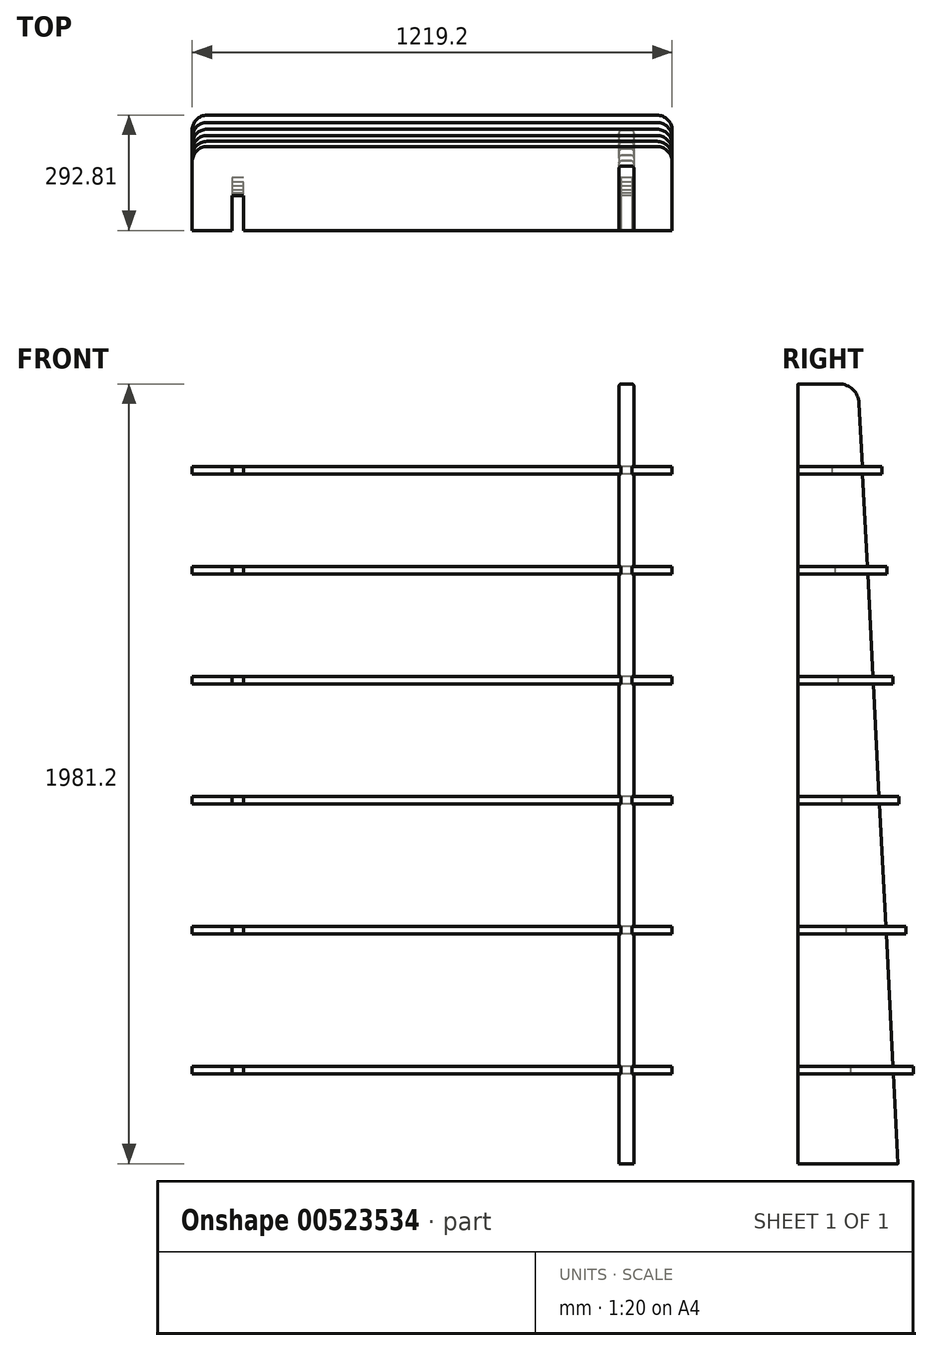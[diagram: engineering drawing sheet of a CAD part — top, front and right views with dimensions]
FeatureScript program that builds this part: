
annotation { "Feature Type Name" : "Feature", "Feature Type Description" : "" }
export const myFeature = defineFeature(function(context is Context, id is Id, definition is map)
    precondition{}
    {
        {
            var Q0;
            Q0=qCreatedBy(makeId("Right.planeOp"),FACE);
            var sketch = newSketch(context, id + "F0", { "sketchPlane" : qUnion([Q0])});
            skLineSegment(sketch, "E0.bottom", {"start": v(-186.04, 1286.69) * mm, "end": v(-81.9, 1286.69) * mm});
            skLineSegment(sketch, "E0.top", {"start": v(-186.04, -694.51) * mm, "end": v(67.96, -694.51) * mm});
            skLineSegment(sketch, "E0.left", {"start": v(-186.04, 1286.69) * mm, "end": v(-186.04, -694.51) * mm});
            skLineSegment(sketch, "E1", {"start": v(56.23, -465.91) * mm, "end": v(-51.72, -465.91) * mm});
            skLineSegment(sketch, "E2", {"start": v(-51.72, -465.91) * mm, "end": v(-51.72, -446.86) * mm});
            skLineSegment(sketch, "E3", {"start": v(-51.72, -446.86) * mm, "end": v(55.26, -446.86) * mm});
            skLineSegment(sketch, "E4.0.1.0", {"start": v(-63.6, -110.31) * mm, "end": v(-63.6, -91.26) * mm});
            skLineSegment(sketch, "E4.0.1.1", {"start": v(38, -110.31) * mm, "end": v(-63.6, -110.31) * mm});
            skLineSegment(sketch, "E4.0.1.2", {"start": v(-63.6, -91.26) * mm, "end": v(37.02, -91.26) * mm});
            skLineSegment(sketch, "E4.0.2.0", {"start": v(-74.19, 219.89) * mm, "end": v(-74.19, 238.94) * mm});
            skLineSegment(sketch, "E4.0.2.1", {"start": v(21.06, 219.89) * mm, "end": v(-74.19, 219.89) * mm});
            skLineSegment(sketch, "E4.0.2.2", {"start": v(-74.19, 238.94) * mm, "end": v(20.09, 238.94) * mm});
            skLineSegment(sketch, "E4.0.3.0", {"start": v(-83.47, 524.69) * mm, "end": v(-83.47, 543.74) * mm});
            skLineSegment(sketch, "E4.0.3.1", {"start": v(5.43, 524.69) * mm, "end": v(-83.47, 524.69) * mm});
            skLineSegment(sketch, "E4.0.3.2", {"start": v(-83.47, 543.74) * mm, "end": v(4.46, 543.74) * mm});
            skLineSegment(sketch, "E4.0.4.0", {"start": v(-91.44, 804.09) * mm, "end": v(-91.44, 823.14) * mm});
            skLineSegment(sketch, "E4.0.4.1", {"start": v(-8.9, 804.09) * mm, "end": v(-91.44, 804.09) * mm});
            skLineSegment(sketch, "E4.0.4.2", {"start": v(-91.44, 823.14) * mm, "end": v(-9.87, 823.14) * mm});
            skLineSegment(sketch, "E4.0.5.0", {"start": v(-98.12, 1058.09) * mm, "end": v(-98.12, 1077.14) * mm});
            skLineSegment(sketch, "E4.0.5.1", {"start": v(-21.92, 1058.09) * mm, "end": v(-98.12, 1058.09) * mm});
            skLineSegment(sketch, "E4.0.5.2", {"start": v(-98.12, 1077.14) * mm, "end": v(-22.9, 1077.14) * mm});
            skLineSegment(sketch, "E5", {"start": v(67.96, -694.51) * mm, "end": v(56.23, -465.91) * mm});
            skLineSegment(sketch, "E6.trimOffspring", {"start": v(-22.9, 1077.14) * mm, "end": v(-31.17, 1238.49) * mm});
            skLineSegment(sketch, "E7.trimOffspring", {"start": v(-9.87, 823.14) * mm, "end": v(-21.92, 1058.09) * mm});
            skLineSegment(sketch, "E8.trimOffspring", {"start": v(4.46, 543.74) * mm, "end": v(-8.9, 804.09) * mm});
            skLineSegment(sketch, "E9.trimOffspring", {"start": v(20.09, 238.94) * mm, "end": v(5.43, 524.69) * mm});
            skLineSegment(sketch, "E10.trimOffspring", {"start": v(37.02, -91.26) * mm, "end": v(21.06, 219.89) * mm});
            skLineSegment(sketch, "E11.trimOffspring", {"start": v(55.26, -446.86) * mm, "end": v(38, -110.31) * mm});
            skPoint(sketch, "E12.visualSharp", {"position": v(-33.64, 1286.69) * mm});
            skArc(sketch, "E12.filletArc", {"start": v(-31.17, 1238.49) * mm, "mid": v(-46.92, 1272.72) * mm, "end": v(-81.9, 1286.69) * mm});
            skSolve(sketch);
        }
        {
            var Q0;
            Q0 = qSketchRegion(id + "F0", true);
            extrude(context, id + "F1", {"entities" : qUnion([Q0]), "depth" : 38.1 * mm, "offsetDistance" : 25.4 * mm});
        }
        {
            var Q0;
            Q0=makeQuery(id+"F1.opExtrude","SWEPT_FACE",FACE,{"disambiguationData":[OSD([sQuery(id+"F0.wireOp",EDGE,"E0.left")])]});
            var sketch = newSketch(context, id + "F2", { "sketchPlane" : qUnion([Q0])});
            skLineSegment(sketch, "E13.bottom", {"start": v(0, 1077.14) * mm, "end": v(4.76, 1077.14) * mm});
            skLineSegment(sketch, "E13.top", {"start": v(0, 1058.09) * mm, "end": v(4.76, 1058.09) * mm});
            skLineSegment(sketch, "E13.left", {"start": v(0, 1077.14) * mm, "end": v(0, 1058.09) * mm});
            skLineSegment(sketch, "E13.right", {"start": v(4.76, 1077.14) * mm, "end": v(4.76, 1058.09) * mm});
            skLineSegment(sketch, "E14.bottom", {"start": v(0, 823.14) * mm, "end": v(4.76, 823.14) * mm});
            skLineSegment(sketch, "E14.top", {"start": v(0, 804.09) * mm, "end": v(4.76, 804.09) * mm});
            skLineSegment(sketch, "E14.left", {"start": v(0, 823.14) * mm, "end": v(0, 804.09) * mm});
            skLineSegment(sketch, "E14.right", {"start": v(4.76, 823.14) * mm, "end": v(4.76, 804.09) * mm});
            skLineSegment(sketch, "E15.bottom", {"start": v(0, 543.74) * mm, "end": v(4.76, 543.74) * mm});
            skLineSegment(sketch, "E15.top", {"start": v(0, 524.69) * mm, "end": v(4.76, 524.69) * mm});
            skLineSegment(sketch, "E15.left", {"start": v(0, 543.74) * mm, "end": v(0, 524.69) * mm});
            skLineSegment(sketch, "E15.right", {"start": v(4.76, 543.74) * mm, "end": v(4.76, 524.69) * mm});
            skLineSegment(sketch, "E16.bottom", {"start": v(0, 238.94) * mm, "end": v(4.76, 238.94) * mm});
            skLineSegment(sketch, "E16.top", {"start": v(0, 219.89) * mm, "end": v(4.76, 219.89) * mm});
            skLineSegment(sketch, "E16.left", {"start": v(0, 238.94) * mm, "end": v(0, 219.89) * mm});
            skLineSegment(sketch, "E16.right", {"start": v(4.76, 238.94) * mm, "end": v(4.76, 219.89) * mm});
            skLineSegment(sketch, "E17.bottom", {"start": v(0, -91.26) * mm, "end": v(4.76, -91.26) * mm});
            skLineSegment(sketch, "E17.top", {"start": v(0, -110.31) * mm, "end": v(4.76, -110.31) * mm});
            skLineSegment(sketch, "E17.left", {"start": v(0, -91.26) * mm, "end": v(0, -110.31) * mm});
            skLineSegment(sketch, "E17.right", {"start": v(4.76, -91.26) * mm, "end": v(4.76, -110.31) * mm});
            skLineSegment(sketch, "E18.bottom", {"start": v(0, -446.86) * mm, "end": v(4.76, -446.86) * mm});
            skLineSegment(sketch, "E18.top", {"start": v(0, -465.91) * mm, "end": v(4.76, -465.91) * mm});
            skLineSegment(sketch, "E18.left", {"start": v(0, -446.86) * mm, "end": v(0, -465.91) * mm});
            skLineSegment(sketch, "E18.right", {"start": v(4.76, -446.86) * mm, "end": v(4.76, -465.91) * mm});
            skLineSegment(sketch, "E19", {"start": v(19.05, 1286.69) * mm, "end": v(19.05, -694.51) * mm, "construction": true});
            skLineSegment(sketch, "E20.MirrorCS", {"start": v(38.1, -465.91) * mm, "end": v(33.34, -465.91) * mm});
            skLineSegment(sketch, "E21.MirrorCS", {"start": v(38.1, -446.86) * mm, "end": v(33.34, -446.86) * mm});
            skLineSegment(sketch, "E22.MirrorCS", {"start": v(33.34, -446.86) * mm, "end": v(33.34, -465.91) * mm});
            skLineSegment(sketch, "E23.MirrorCS", {"start": v(38.1, -446.86) * mm, "end": v(38.1, -465.91) * mm});
            skLineSegment(sketch, "E24.MirrorCS", {"start": v(38.1, -110.31) * mm, "end": v(33.34, -110.31) * mm});
            skLineSegment(sketch, "E25.MirrorCS", {"start": v(38.1, -91.26) * mm, "end": v(33.34, -91.26) * mm});
            skLineSegment(sketch, "E26.MirrorCS", {"start": v(33.34, -91.26) * mm, "end": v(33.34, -110.31) * mm});
            skLineSegment(sketch, "E27.MirrorCS", {"start": v(38.1, -91.26) * mm, "end": v(38.1, -110.31) * mm});
            skLineSegment(sketch, "E28.MirrorCS", {"start": v(38.1, 219.89) * mm, "end": v(33.34, 219.89) * mm});
            skLineSegment(sketch, "E29.MirrorCS", {"start": v(38.1, 238.94) * mm, "end": v(33.34, 238.94) * mm});
            skLineSegment(sketch, "E30.MirrorCS", {"start": v(38.1, 238.94) * mm, "end": v(38.1, 219.89) * mm});
            skLineSegment(sketch, "E31.MirrorCS", {"start": v(33.34, 238.94) * mm, "end": v(33.34, 219.89) * mm});
            skLineSegment(sketch, "E32.MirrorCS", {"start": v(38.1, 543.74) * mm, "end": v(33.34, 543.74) * mm});
            skLineSegment(sketch, "E33.MirrorCS", {"start": v(38.1, 524.69) * mm, "end": v(33.34, 524.69) * mm});
            skLineSegment(sketch, "E34.MirrorCS", {"start": v(38.1, 543.74) * mm, "end": v(38.1, 524.69) * mm});
            skLineSegment(sketch, "E35.MirrorCS", {"start": v(33.34, 543.74) * mm, "end": v(33.34, 524.69) * mm});
            skLineSegment(sketch, "E36.MirrorCS", {"start": v(38.1, 823.14) * mm, "end": v(33.34, 823.14) * mm});
            skLineSegment(sketch, "E37.MirrorCS", {"start": v(38.1, 804.09) * mm, "end": v(33.34, 804.09) * mm});
            skLineSegment(sketch, "E38.MirrorCS", {"start": v(38.1, 823.14) * mm, "end": v(38.1, 804.09) * mm});
            skLineSegment(sketch, "E39.MirrorCS", {"start": v(33.34, 823.14) * mm, "end": v(33.34, 804.09) * mm});
            skLineSegment(sketch, "E40.MirrorCS", {"start": v(38.1, 1077.14) * mm, "end": v(33.34, 1077.14) * mm});
            skLineSegment(sketch, "E41.MirrorCS", {"start": v(38.1, 1058.09) * mm, "end": v(33.34, 1058.09) * mm});
            skLineSegment(sketch, "E42.MirrorCS", {"start": v(33.34, 1077.14) * mm, "end": v(33.34, 1058.09) * mm});
            skLineSegment(sketch, "E43.MirrorCS", {"start": v(38.1, 1077.14) * mm, "end": v(38.1, 1058.09) * mm});
            skSolve(sketch);
        }
        {
            var Q0;
            Q0 = qSketchRegion(id + "F2", true);
            extrude(context, id + "F3", {"entities" : qUnion([Q0]), "operationType" : NewBodyOperationType.REMOVE, "endBound" : BoundingType.UP_TO_NEXT, "oppositeDirection" : true, "depth" : 25.4 * mm, "offsetDistance" : 25.4 * mm});
        }
        {
            var Q0;
            Q0=makeQuery(id+"F3.boolean.opBoolean","MERGE",FACE,{"derivedFrom":[makeQuery(id+"F1.opExtrude","SWEPT_FACE",FACE,{"disambiguationData":[OSD([sQuery(id+"F0.wireOp",EDGE,"E1")])]}),makeQuery(id+"F3.opExtrude","SWEPT_FACE",FACE,{"disambiguationData":[OSD([sQuery(id+"F2.wireOp",EDGE,"E18.top")])]}),makeQuery(id+"F3.opExtrude","SWEPT_FACE",FACE,{"disambiguationData":[OSD([sQuery(id+"F2.wireOp",EDGE,"E20.MirrorCS")])]})]});
            var sketch = newSketch(context, id + "F4", { "sketchPlane" : qUnion([Q0])});
            skLineSegment(sketch, "E44.bottom", {"start": v(134.94, -186.04) * mm, "end": v(33.34, -186.04) * mm});
            skLineSegment(sketch, "E44.top", {"start": v(96.84, 106.77) * mm, "end": v(-474.66, 106.77) * mm});
            skLineSegment(sketch, "E44.left", {"start": v(134.94, -186.04) * mm, "end": v(134.94, 68.67) * mm});
            skLineSegment(sketch, "E44.right", {"start": v(-474.66, -186.04) * mm, "end": v(-474.66, 106.77) * mm, "construction": true});
            skPoint(sketch, "E45.visualSharp", {"position": v(134.94, 106.77) * mm});
            skArc(sketch, "E45.filletArc", {"start": v(134.94, 68.67) * mm, "mid": v(123.78, 95.6) * mm, "end": v(96.84, 106.77) * mm});
            skLineSegment(sketch, "E46", {"start": v(4.76, -186.04) * mm, "end": v(4.76, -51.72) * mm});
            skLineSegment(sketch, "E47", {"start": v(4.76, -51.72) * mm, "end": v(33.34, -51.72) * mm});
            skLineSegment(sketch, "E48", {"start": v(33.34, -51.72) * mm, "end": v(33.34, -186.04) * mm});
            skLineSegment(sketch, "E49.trimOffspring", {"start": v(4.76, -186.04) * mm, "end": v(-474.66, -186.04) * mm});
            skLineSegment(sketch, "E50.MirrorCS", {"start": v(-954.09, -51.72) * mm, "end": v(-982.66, -51.72) * mm});
            skArc(sketch, "E51.MirrorCS", {"start": v(-1084.26, 68.67) * mm, "mid": v(-1073.1, 95.6) * mm, "end": v(-1046.16, 106.77) * mm});
            skLineSegment(sketch, "E52.MirrorCS", {"start": v(-954.09, -186.04) * mm, "end": v(-474.66, -186.04) * mm});
            skLineSegment(sketch, "E53.MirrorCS", {"start": v(-982.66, -51.72) * mm, "end": v(-982.66, -186.04) * mm});
            skPoint(sketch, "E54.MirrorP", {"position": v(-1084.26, 106.77) * mm});
            skLineSegment(sketch, "E55.MirrorCS", {"start": v(-1084.26, -186.04) * mm, "end": v(-982.66, -186.04) * mm});
            skLineSegment(sketch, "E56.MirrorCS", {"start": v(-1084.26, -186.04) * mm, "end": v(-1084.26, 68.67) * mm});
            skLineSegment(sketch, "E57.MirrorCS", {"start": v(-1046.16, 106.77) * mm, "end": v(-474.66, 106.77) * mm});
            skLineSegment(sketch, "E58.MirrorCS", {"start": v(-954.09, -186.04) * mm, "end": v(-954.09, -51.72) * mm});
            skSolve(sketch);
        }
        {
            var Q0;
            Q0 = qSketchRegion(id + "F4", true);
            var Q1;
            Q1=makeQuery(id+"F3.boolean.opBoolean","MERGE",FACE,{"derivedFrom":[makeQuery(id+"F1.opExtrude","SWEPT_FACE",FACE,{"disambiguationData":[OSD([sQuery(id+"F0.wireOp",EDGE,"E3")])]}),makeQuery(id+"F3.opExtrude","SWEPT_FACE",FACE,{"disambiguationData":[OSD([sQuery(id+"F2.wireOp",EDGE,"E18.bottom")])]}),makeQuery(id+"F3.opExtrude","SWEPT_FACE",FACE,{"disambiguationData":[OSD([sQuery(id+"F2.wireOp",EDGE,"E21.MirrorCS")])]})]});
            extrude(context, id + "F5", {"entities" : qUnion([Q0]), "endBound" : BoundingType.UP_TO_SURFACE, "depth" : 25.4 * mm, "endBoundEntityFace" : qUnion([Q1]), "offsetDistance" : 25.4 * mm});
        }
        {
            var Q0;
            Q0=makeQuery(id+"F3.boolean.opBoolean","MERGE",FACE,{"derivedFrom":[makeQuery(id+"F1.opExtrude","SWEPT_FACE",FACE,{"disambiguationData":[OSD([sQuery(id+"F0.wireOp",EDGE,"E4.0.1.1")])]}),makeQuery(id+"F3.opExtrude","SWEPT_FACE",FACE,{"disambiguationData":[OSD([sQuery(id+"F2.wireOp",EDGE,"E17.top")])]}),makeQuery(id+"F3.opExtrude","SWEPT_FACE",FACE,{"disambiguationData":[OSD([sQuery(id+"F2.wireOp",EDGE,"E24.MirrorCS")])]})]});
            var sketch = newSketch(context, id + "F6", { "sketchPlane" : qUnion([Q0])});
            skLineSegment(sketch, "E59.bottom", {"start": v(134.94, -186.04) * mm, "end": v(33.34, -186.04) * mm});
            skLineSegment(sketch, "E59.top", {"start": v(96.84, 88.12) * mm, "end": v(-474.66, 88.12) * mm});
            skLineSegment(sketch, "E59.left", {"start": v(134.94, -186.04) * mm, "end": v(134.94, 50.02) * mm});
            skLineSegment(sketch, "E59.right", {"start": v(-474.66, -186.04) * mm, "end": v(-474.66, 88.12) * mm, "construction": true});
            skLineSegment(sketch, "E60", {"start": v(4.76, -186.04) * mm, "end": v(4.76, -63.6) * mm});
            skLineSegment(sketch, "E61", {"start": v(4.76, -63.6) * mm, "end": v(33.34, -63.6) * mm});
            skLineSegment(sketch, "E62", {"start": v(33.34, -63.6) * mm, "end": v(33.34, -186.04) * mm});
            skLineSegment(sketch, "E63.trimOffspring", {"start": v(4.76, -186.04) * mm, "end": v(-474.66, -186.04) * mm});
            skLineSegment(sketch, "E64.MirrorCS", {"start": v(-954.09, -63.6) * mm, "end": v(-982.66, -63.6) * mm});
            skLineSegment(sketch, "E65.MirrorCS", {"start": v(-1084.26, -186.04) * mm, "end": v(-982.66, -186.04) * mm});
            skLineSegment(sketch, "E66.MirrorCS", {"start": v(-1046.16, 88.12) * mm, "end": v(-474.66, 88.12) * mm});
            skLineSegment(sketch, "E67.MirrorCS", {"start": v(-1084.26, -186.04) * mm, "end": v(-1084.26, 50.02) * mm});
            skLineSegment(sketch, "E68.MirrorCS", {"start": v(-954.09, -186.04) * mm, "end": v(-474.66, -186.04) * mm});
            skLineSegment(sketch, "E69.MirrorCS", {"start": v(-982.66, -63.6) * mm, "end": v(-982.66, -186.04) * mm});
            skLineSegment(sketch, "E70.MirrorCS", {"start": v(-954.09, -186.04) * mm, "end": v(-954.09, -63.6) * mm});
            skPoint(sketch, "E71.visualSharp", {"position": v(134.94, 88.12) * mm});
            skArc(sketch, "E71.filletArc", {"start": v(134.94, 50.02) * mm, "mid": v(123.78, 76.96) * mm, "end": v(96.84, 88.12) * mm});
            skPoint(sketch, "E72.visualSharp", {"position": v(-1084.26, 88.12) * mm});
            skArc(sketch, "E72.filletArc", {"start": v(-1046.16, 88.12) * mm, "mid": v(-1073.1, 76.96) * mm, "end": v(-1084.26, 50.02) * mm});
            skSolve(sketch);
        }
        {
            var Q0;
            Q0 = qSketchRegion(id + "F6", true);
            var Q1;
            Q1=makeQuery(id+"F3.boolean.opBoolean","MERGE",FACE,{"derivedFrom":[makeQuery(id+"F1.opExtrude","SWEPT_FACE",FACE,{"disambiguationData":[OSD([sQuery(id+"F0.wireOp",EDGE,"E4.0.1.2")])]}),makeQuery(id+"F3.opExtrude","SWEPT_FACE",FACE,{"disambiguationData":[OSD([sQuery(id+"F2.wireOp",EDGE,"E17.bottom")])]}),makeQuery(id+"F3.opExtrude","SWEPT_FACE",FACE,{"disambiguationData":[OSD([sQuery(id+"F2.wireOp",EDGE,"E25.MirrorCS")])]})]});
            extrude(context, id + "F7", {"entities" : qUnion([Q0]), "endBound" : BoundingType.UP_TO_SURFACE, "depth" : 25.4 * mm, "endBoundEntityFace" : qUnion([Q1]), "offsetDistance" : 25.4 * mm});
        }
        {
            var Q0;
            Q0=makeQuery(id+"F3.boolean.opBoolean","MERGE",FACE,{"derivedFrom":[makeQuery(id+"F1.opExtrude","SWEPT_FACE",FACE,{"disambiguationData":[OSD([sQuery(id+"F0.wireOp",EDGE,"E4.0.2.1")])]}),makeQuery(id+"F3.opExtrude","SWEPT_FACE",FACE,{"disambiguationData":[OSD([sQuery(id+"F2.wireOp",EDGE,"E16.top")])]}),makeQuery(id+"F3.opExtrude","SWEPT_FACE",FACE,{"disambiguationData":[OSD([sQuery(id+"F2.wireOp",EDGE,"E28.MirrorCS")])]})]});
            var sketch = newSketch(context, id + "F8", { "sketchPlane" : qUnion([Q0])});
            skLineSegment(sketch, "E73.bottom", {"start": v(134.94, -186.04) * mm, "end": v(33.34, -186.04) * mm});
            skLineSegment(sketch, "E73.top", {"start": v(96.84, 70.83) * mm, "end": v(-474.66, 70.83) * mm});
            skLineSegment(sketch, "E73.left", {"start": v(134.94, -186.04) * mm, "end": v(134.94, 32.73) * mm});
            skLineSegment(sketch, "E73.right", {"start": v(-474.66, -186.04) * mm, "end": v(-474.66, 70.83) * mm, "construction": true});
            skLineSegment(sketch, "E74", {"start": v(4.76, -186.04) * mm, "end": v(4.76, -74.19) * mm});
            skLineSegment(sketch, "E75", {"start": v(4.76, -74.19) * mm, "end": v(33.34, -74.19) * mm});
            skLineSegment(sketch, "E76", {"start": v(33.34, -74.19) * mm, "end": v(33.34, -186.04) * mm});
            skLineSegment(sketch, "E77.trimOffspring", {"start": v(4.76, -186.04) * mm, "end": v(-474.66, -186.04) * mm});
            skPoint(sketch, "E78.visualSharp", {"position": v(134.94, 70.83) * mm});
            skArc(sketch, "E78.filletArc", {"start": v(134.94, 32.73) * mm, "mid": v(123.78, 59.67) * mm, "end": v(96.84, 70.83) * mm});
            skLineSegment(sketch, "E79.MirrorCS", {"start": v(-954.09, -74.19) * mm, "end": v(-982.66, -74.19) * mm});
            skLineSegment(sketch, "E80.MirrorCS", {"start": v(-982.66, -74.19) * mm, "end": v(-982.66, -186.04) * mm});
            skLineSegment(sketch, "E81.MirrorCS", {"start": v(-954.09, -186.04) * mm, "end": v(-474.66, -186.04) * mm});
            skArc(sketch, "E82.MirrorCS", {"start": v(-1084.26, 32.73) * mm, "mid": v(-1073.1, 59.67) * mm, "end": v(-1046.16, 70.83) * mm});
            skLineSegment(sketch, "E83.MirrorCS", {"start": v(-1084.26, -186.04) * mm, "end": v(-982.66, -186.04) * mm});
            skLineSegment(sketch, "E84.MirrorCS", {"start": v(-1046.16, 70.83) * mm, "end": v(-474.66, 70.83) * mm});
            skLineSegment(sketch, "E85.MirrorCS", {"start": v(-1084.26, -186.04) * mm, "end": v(-1084.26, 32.73) * mm});
            skPoint(sketch, "E86.MirrorP", {"position": v(-1084.26, 70.83) * mm});
            skLineSegment(sketch, "E87.MirrorCS", {"start": v(-954.09, -186.04) * mm, "end": v(-954.09, -74.19) * mm});
            skSolve(sketch);
        }
        {
            var Q0;
            Q0 = qSketchRegion(id + "F8", true);
            var Q1;
            Q1=makeQuery(id+"F3.boolean.opBoolean","MERGE",FACE,{"derivedFrom":[makeQuery(id+"F1.opExtrude","SWEPT_FACE",FACE,{"disambiguationData":[OSD([sQuery(id+"F0.wireOp",EDGE,"E4.0.2.2")])]}),makeQuery(id+"F3.opExtrude","SWEPT_FACE",FACE,{"disambiguationData":[OSD([sQuery(id+"F2.wireOp",EDGE,"E16.bottom")])]}),makeQuery(id+"F3.opExtrude","SWEPT_FACE",FACE,{"disambiguationData":[OSD([sQuery(id+"F2.wireOp",EDGE,"E29.MirrorCS")])]})]});
            extrude(context, id + "F9", {"entities" : qUnion([Q0]), "endBound" : BoundingType.UP_TO_SURFACE, "depth" : 25.4 * mm, "endBoundEntityFace" : qUnion([Q1]), "offsetDistance" : 25.4 * mm});
        }
        {
            var Q0;
            Q0=makeQuery(id+"F3.boolean.opBoolean","MERGE",FACE,{"derivedFrom":[makeQuery(id+"F1.opExtrude","SWEPT_FACE",FACE,{"disambiguationData":[OSD([sQuery(id+"F0.wireOp",EDGE,"E4.0.3.1")])]}),makeQuery(id+"F3.opExtrude","SWEPT_FACE",FACE,{"disambiguationData":[OSD([sQuery(id+"F2.wireOp",EDGE,"E15.top")])]}),makeQuery(id+"F3.opExtrude","SWEPT_FACE",FACE,{"disambiguationData":[OSD([sQuery(id+"F2.wireOp",EDGE,"E33.MirrorCS")])]})]});
            var sketch = newSketch(context, id + "F10", { "sketchPlane" : qUnion([Q0])});
            skLineSegment(sketch, "E88.bottom", {"start": v(134.94, -186.04) * mm, "end": v(33.34, -186.04) * mm});
            skLineSegment(sketch, "E88.top", {"start": v(96.84, 54.85) * mm, "end": v(-474.66, 54.85) * mm});
            skLineSegment(sketch, "E88.left", {"start": v(134.94, -186.04) * mm, "end": v(134.94, 16.75) * mm});
            skLineSegment(sketch, "E88.right", {"start": v(-474.66, -186.04) * mm, "end": v(-474.66, 54.85) * mm, "construction": true});
            skPoint(sketch, "E89.visualSharp", {"position": v(134.94, 54.85) * mm});
            skArc(sketch, "E89.filletArc", {"start": v(134.94, 16.75) * mm, "mid": v(123.78, 43.7) * mm, "end": v(96.84, 54.85) * mm});
            skLineSegment(sketch, "E90", {"start": v(4.76, -186.04) * mm, "end": v(4.76, -83.47) * mm});
            skLineSegment(sketch, "E91", {"start": v(4.76, -83.47) * mm, "end": v(33.34, -83.47) * mm});
            skLineSegment(sketch, "E92", {"start": v(33.34, -83.47) * mm, "end": v(33.34, -186.04) * mm});
            skLineSegment(sketch, "E93.trimOffspring", {"start": v(4.76, -186.04) * mm, "end": v(-474.66, -186.04) * mm});
            skLineSegment(sketch, "E94.MirrorCS", {"start": v(-954.09, -83.47) * mm, "end": v(-982.66, -83.47) * mm});
            skArc(sketch, "E95.MirrorCS", {"start": v(-1084.26, 16.75) * mm, "mid": v(-1073.1, 43.7) * mm, "end": v(-1046.16, 54.85) * mm});
            skLineSegment(sketch, "E96.MirrorCS", {"start": v(-1084.26, -186.04) * mm, "end": v(-1084.26, 16.75) * mm});
            skLineSegment(sketch, "E97.MirrorCS", {"start": v(-1046.16, 54.85) * mm, "end": v(-474.66, 54.85) * mm});
            skLineSegment(sketch, "E98.MirrorCS", {"start": v(-1084.26, -186.04) * mm, "end": v(-982.66, -186.04) * mm});
            skLineSegment(sketch, "E99.MirrorCS", {"start": v(-954.09, -186.04) * mm, "end": v(-954.09, -83.47) * mm});
            skLineSegment(sketch, "E100.MirrorCS", {"start": v(-982.66, -83.47) * mm, "end": v(-982.66, -186.04) * mm});
            skLineSegment(sketch, "E101.MirrorCS", {"start": v(-954.09, -186.04) * mm, "end": v(-474.66, -186.04) * mm});
            skPoint(sketch, "E102.MirrorP", {"position": v(-1084.26, 54.85) * mm});
            skSolve(sketch);
        }
        {
            var Q0;
            Q0 = qSketchRegion(id + "F10", true);
            var Q1;
            Q1=makeQuery(id+"F3.boolean.opBoolean","MERGE",FACE,{"derivedFrom":[makeQuery(id+"F1.opExtrude","SWEPT_FACE",FACE,{"disambiguationData":[OSD([sQuery(id+"F0.wireOp",EDGE,"E4.0.3.2")])]}),makeQuery(id+"F3.opExtrude","SWEPT_FACE",FACE,{"disambiguationData":[OSD([sQuery(id+"F2.wireOp",EDGE,"E15.bottom")])]}),makeQuery(id+"F3.opExtrude","SWEPT_FACE",FACE,{"disambiguationData":[OSD([sQuery(id+"F2.wireOp",EDGE,"E32.MirrorCS")])]})]});
            extrude(context, id + "F11", {"entities" : qUnion([Q0]), "endBound" : BoundingType.UP_TO_SURFACE, "depth" : 25.4 * mm, "endBoundEntityFace" : qUnion([Q1]), "offsetDistance" : 25.4 * mm});
        }
        {
            var Q0;
            Q0=makeQuery(id+"F3.boolean.opBoolean","MERGE",FACE,{"derivedFrom":[makeQuery(id+"F1.opExtrude","SWEPT_FACE",FACE,{"disambiguationData":[OSD([sQuery(id+"F0.wireOp",EDGE,"E4.0.4.1")])]}),makeQuery(id+"F3.opExtrude","SWEPT_FACE",FACE,{"disambiguationData":[OSD([sQuery(id+"F2.wireOp",EDGE,"E14.top")])]}),makeQuery(id+"F3.opExtrude","SWEPT_FACE",FACE,{"disambiguationData":[OSD([sQuery(id+"F2.wireOp",EDGE,"E37.MirrorCS")])]})]});
            var sketch = newSketch(context, id + "F12", { "sketchPlane" : qUnion([Q0])});
            skLineSegment(sketch, "E103.bottom", {"start": v(134.94, -186.04) * mm, "end": v(33.34, -186.04) * mm});
            skLineSegment(sketch, "E103.top", {"start": v(96.84, 40.2) * mm, "end": v(-474.66, 40.2) * mm});
            skLineSegment(sketch, "E103.left", {"start": v(134.94, -186.04) * mm, "end": v(134.94, 2.1) * mm});
            skLineSegment(sketch, "E103.right", {"start": v(-474.66, -186.04) * mm, "end": v(-474.66, 40.2) * mm, "construction": true});
            skPoint(sketch, "E104.visualSharp", {"position": v(134.94, 40.2) * mm});
            skArc(sketch, "E104.filletArc", {"start": v(134.94, 2.1) * mm, "mid": v(123.78, 29.04) * mm, "end": v(96.84, 40.2) * mm});
            skLineSegment(sketch, "E105", {"start": v(4.76, -186.04) * mm, "end": v(4.76, -91.44) * mm});
            skLineSegment(sketch, "E106", {"start": v(4.76, -91.44) * mm, "end": v(33.34, -91.44) * mm});
            skLineSegment(sketch, "E107", {"start": v(33.34, -91.44) * mm, "end": v(33.34, -186.04) * mm});
            skLineSegment(sketch, "E108.trimOffspring", {"start": v(4.76, -186.04) * mm, "end": v(-474.66, -186.04) * mm});
            skLineSegment(sketch, "E109.MirrorCS", {"start": v(-954.09, -91.44) * mm, "end": v(-982.66, -91.44) * mm});
            skLineSegment(sketch, "E110.MirrorCS", {"start": v(-954.09, -186.04) * mm, "end": v(-474.66, -186.04) * mm});
            skLineSegment(sketch, "E111.MirrorCS", {"start": v(-982.66, -91.44) * mm, "end": v(-982.66, -186.04) * mm});
            skArc(sketch, "E112.MirrorCS", {"start": v(-1084.26, 2.1) * mm, "mid": v(-1073.1, 29.04) * mm, "end": v(-1046.16, 40.2) * mm});
            skLineSegment(sketch, "E113.MirrorCS", {"start": v(-1084.26, -186.04) * mm, "end": v(-982.66, -186.04) * mm});
            skLineSegment(sketch, "E114.MirrorCS", {"start": v(-1046.16, 40.2) * mm, "end": v(-474.66, 40.2) * mm});
            skLineSegment(sketch, "E115.MirrorCS", {"start": v(-1084.26, -186.04) * mm, "end": v(-1084.26, 2.1) * mm});
            skLineSegment(sketch, "E116.MirrorCS", {"start": v(-954.09, -186.04) * mm, "end": v(-954.09, -91.44) * mm});
            skPoint(sketch, "E117.MirrorP", {"position": v(-1084.26, 40.2) * mm});
            skSolve(sketch);
        }
        {
            var Q0;
            Q0 = qSketchRegion(id + "F12", true);
            var Q1;
            Q1=makeQuery(id+"F3.boolean.opBoolean","MERGE",FACE,{"derivedFrom":[makeQuery(id+"F1.opExtrude","SWEPT_FACE",FACE,{"disambiguationData":[OSD([sQuery(id+"F0.wireOp",EDGE,"E4.0.4.2")])]}),makeQuery(id+"F3.opExtrude","SWEPT_FACE",FACE,{"disambiguationData":[OSD([sQuery(id+"F2.wireOp",EDGE,"E14.bottom")])]}),makeQuery(id+"F3.opExtrude","SWEPT_FACE",FACE,{"disambiguationData":[OSD([sQuery(id+"F2.wireOp",EDGE,"E36.MirrorCS")])]})]});
            extrude(context, id + "F13", {"entities" : qUnion([Q0]), "endBound" : BoundingType.UP_TO_SURFACE, "depth" : 25.4 * mm, "endBoundEntityFace" : qUnion([Q1]), "offsetDistance" : 25.4 * mm});
        }
        {
            var Q0;
            Q0=makeQuery(id+"F3.boolean.opBoolean","MERGE",FACE,{"derivedFrom":[makeQuery(id+"F1.opExtrude","SWEPT_FACE",FACE,{"disambiguationData":[OSD([sQuery(id+"F0.wireOp",EDGE,"E4.0.5.1")])]}),makeQuery(id+"F3.opExtrude","SWEPT_FACE",FACE,{"disambiguationData":[OSD([sQuery(id+"F2.wireOp",EDGE,"E13.top")])]}),makeQuery(id+"F3.opExtrude","SWEPT_FACE",FACE,{"disambiguationData":[OSD([sQuery(id+"F2.wireOp",EDGE,"E41.MirrorCS")])]})]});
            var sketch = newSketch(context, id + "F14", { "sketchPlane" : qUnion([Q0])});
            skLineSegment(sketch, "E118.bottom", {"start": v(134.94, -186.04) * mm, "end": v(33.34, -186.04) * mm});
            skLineSegment(sketch, "E118.top", {"start": v(96.84, 26.88) * mm, "end": v(-474.66, 26.88) * mm});
            skLineSegment(sketch, "E118.left", {"start": v(134.94, -186.04) * mm, "end": v(134.94, -11.22) * mm});
            skLineSegment(sketch, "E118.right", {"start": v(-474.66, -186.04) * mm, "end": v(-474.66, 26.88) * mm, "construction": true});
            skPoint(sketch, "E119.visualSharp", {"position": v(134.94, 26.88) * mm});
            skArc(sketch, "E119.filletArc", {"start": v(134.94, -11.22) * mm, "mid": v(123.78, 15.73) * mm, "end": v(96.84, 26.88) * mm});
            skLineSegment(sketch, "E120", {"start": v(4.76, -186.04) * mm, "end": v(4.76, -98.12) * mm});
            skLineSegment(sketch, "E121", {"start": v(4.76, -98.12) * mm, "end": v(33.34, -98.12) * mm});
            skLineSegment(sketch, "E122", {"start": v(33.34, -98.12) * mm, "end": v(33.34, -186.04) * mm});
            skLineSegment(sketch, "E123.trimOffspring", {"start": v(4.76, -186.04) * mm, "end": v(-474.66, -186.04) * mm});
            skLineSegment(sketch, "E124.MirrorCS", {"start": v(-954.09, -98.12) * mm, "end": v(-982.66, -98.12) * mm});
            skLineSegment(sketch, "E125.MirrorCS", {"start": v(-954.09, -186.04) * mm, "end": v(-954.09, -98.12) * mm});
            skArc(sketch, "E126.MirrorCS", {"start": v(-1084.26, -11.22) * mm, "mid": v(-1073.1, 15.73) * mm, "end": v(-1046.16, 26.88) * mm});
            skLineSegment(sketch, "E127.MirrorCS", {"start": v(-982.66, -98.12) * mm, "end": v(-982.66, -186.04) * mm});
            skLineSegment(sketch, "E128.MirrorCS", {"start": v(-954.09, -186.04) * mm, "end": v(-474.66, -186.04) * mm});
            skLineSegment(sketch, "E129.MirrorCS", {"start": v(-1084.26, -186.04) * mm, "end": v(-982.66, -186.04) * mm});
            skLineSegment(sketch, "E130.MirrorCS", {"start": v(-1046.16, 26.88) * mm, "end": v(-474.66, 26.88) * mm});
            skPoint(sketch, "E131.MirrorP", {"position": v(-1084.26, 26.88) * mm});
            skLineSegment(sketch, "E132.MirrorCS", {"start": v(-1084.26, -186.04) * mm, "end": v(-1084.26, -11.22) * mm});
            skSolve(sketch);
        }
        {
            var Q0;
            Q0 = qSketchRegion(id + "F14", true);
            var Q1;
            Q1=makeQuery(id+"F3.boolean.opBoolean","MERGE",FACE,{"derivedFrom":[makeQuery(id+"F1.opExtrude","SWEPT_FACE",FACE,{"disambiguationData":[OSD([sQuery(id+"F0.wireOp",EDGE,"E4.0.5.2")])]}),makeQuery(id+"F3.opExtrude","SWEPT_FACE",FACE,{"disambiguationData":[OSD([sQuery(id+"F2.wireOp",EDGE,"E13.bottom")])]}),makeQuery(id+"F3.opExtrude","SWEPT_FACE",FACE,{"disambiguationData":[OSD([sQuery(id+"F2.wireOp",EDGE,"E40.MirrorCS")])]})]});
            extrude(context, id + "F15", {"entities" : qUnion([Q0]), "endBound" : BoundingType.UP_TO_SURFACE, "depth" : 25.4 * mm, "endBoundEntityFace" : qUnion([Q1]), "offsetDistance" : 25.4 * mm});
        }
        {
            var Q0;
            Q0=makeQuery(id+"F1.opExtrude","CAP_EDGE",EDGE,{"disambiguationData":[OSD([sQuery(id+"F0.wireOp",EDGE,"E0.bottom")])],"isStart":true});
            var Q1;
            Q1=makeQuery(id+"F1.opExtrude","CAP_EDGE",EDGE,{"disambiguationData":[OSD([sQuery(id+"F0.wireOp",EDGE,"E12.filletArc")])],"isStart":true});
            var Q2;
            Q2=makeQuery(id+"F1.opExtrude","CAP_EDGE",EDGE,{"disambiguationData":[OSD([sQuery(id+"F0.wireOp",EDGE,"E6.trimOffspring")])],"isStart":true});
            var Q3;
            Q3=makeQuery(id+"F1.opExtrude","CAP_EDGE",EDGE,{"disambiguationData":[OSD([sQuery(id+"F0.wireOp",EDGE,"E7.trimOffspring")])],"isStart":true});
            var Q4;
            Q4=makeQuery(id+"F1.opExtrude","CAP_EDGE",EDGE,{"disambiguationData":[OSD([sQuery(id+"F0.wireOp",EDGE,"E8.trimOffspring")])],"isStart":true});
            var Q5;
            Q5=makeQuery(id+"F1.opExtrude","CAP_EDGE",EDGE,{"disambiguationData":[OSD([sQuery(id+"F0.wireOp",EDGE,"E9.trimOffspring")])],"isStart":true});
            var Q6;
            Q6=makeQuery(id+"F1.opExtrude","CAP_EDGE",EDGE,{"disambiguationData":[OSD([sQuery(id+"F0.wireOp",EDGE,"E10.trimOffspring")])],"isStart":true});
            var Q7;
            Q7=makeQuery(id+"F1.opExtrude","CAP_EDGE",EDGE,{"disambiguationData":[OSD([sQuery(id+"F0.wireOp",EDGE,"E11.trimOffspring")])],"isStart":true});
            var Q8;
            Q8=makeQuery(id+"F1.opExtrude","CAP_EDGE",EDGE,{"disambiguationData":[OSD([sQuery(id+"F0.wireOp",EDGE,"E5")])],"isStart":true});
            var Q9;
            Q9=makeQuery(id+"F1.opExtrude","CAP_EDGE",EDGE,{"disambiguationData":[OSD([sQuery(id+"F0.wireOp",EDGE,"E5")])],"isStart":false});
            var Q10;
            Q10=makeQuery(id+"F1.opExtrude","CAP_EDGE",EDGE,{"disambiguationData":[OSD([sQuery(id+"F0.wireOp",EDGE,"E11.trimOffspring")])],"isStart":false});
            var Q11;
            Q11=makeQuery(id+"F1.opExtrude","CAP_EDGE",EDGE,{"disambiguationData":[OSD([sQuery(id+"F0.wireOp",EDGE,"E10.trimOffspring")])],"isStart":false});
            var Q12;
            Q12=makeQuery(id+"F1.opExtrude","CAP_EDGE",EDGE,{"disambiguationData":[OSD([sQuery(id+"F0.wireOp",EDGE,"E9.trimOffspring")])],"isStart":false});
            var Q13;
            Q13=makeQuery(id+"F1.opExtrude","CAP_EDGE",EDGE,{"disambiguationData":[OSD([sQuery(id+"F0.wireOp",EDGE,"E8.trimOffspring")])],"isStart":false});
            var Q14;
            Q14=makeQuery(id+"F1.opExtrude","CAP_EDGE",EDGE,{"disambiguationData":[OSD([sQuery(id+"F0.wireOp",EDGE,"E7.trimOffspring")])],"isStart":false});
            var Q15;
            Q15=makeQuery(id+"F1.opExtrude","CAP_EDGE",EDGE,{"disambiguationData":[OSD([sQuery(id+"F0.wireOp",EDGE,"E6.trimOffspring")])],"isStart":false});
            var Q16;
            Q16=makeQuery(id+"F1.opExtrude","CAP_EDGE",EDGE,{"disambiguationData":[OSD([sQuery(id+"F0.wireOp",EDGE,"E12.filletArc")])],"isStart":false});
            var Q17;
            Q17=makeQuery(id+"F1.opExtrude","CAP_EDGE",EDGE,{"disambiguationData":[OSD([sQuery(id+"F0.wireOp",EDGE,"E0.bottom")])],"isStart":false});
            fillet(context, id + "F16", {"entities" : qUnion([Q0, Q1, Q2, Q3, Q4, Q5, Q6, Q7, Q8, Q9, Q10, Q11, Q12, Q13, Q14, Q15, Q16, Q17]), "radius" : 6.35 * mm, "tangentPropagation" : true, "allowEdgeOverflow" : false});
        }
    });
